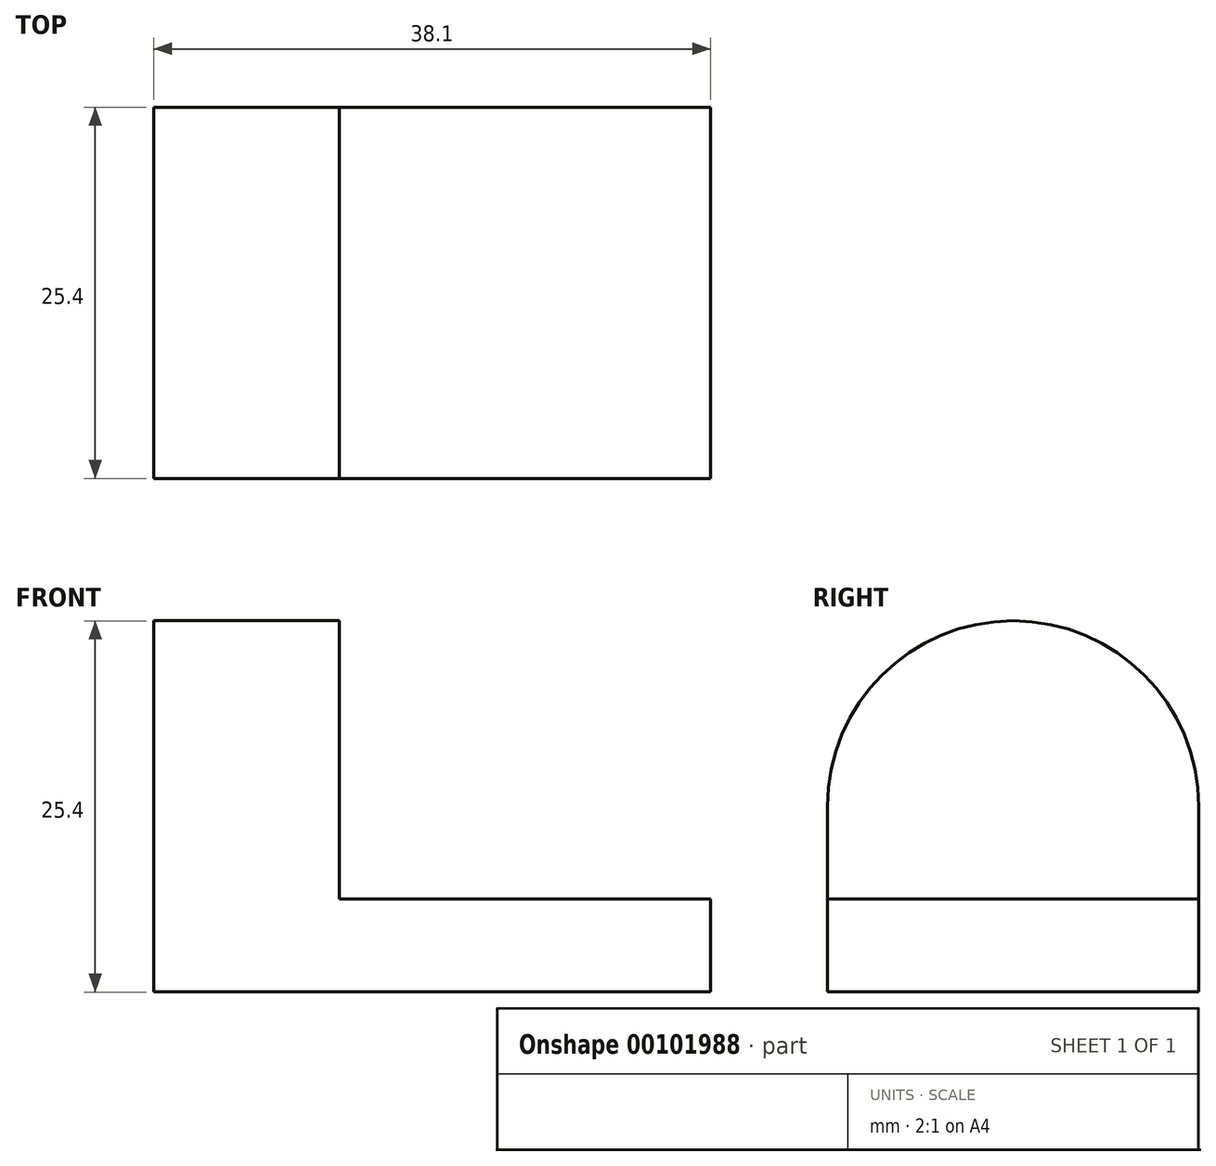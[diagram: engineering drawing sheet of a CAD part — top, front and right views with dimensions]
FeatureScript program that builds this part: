
annotation { "Feature Type Name" : "Feature", "Feature Type Description" : "" }
export const myFeature = defineFeature(function(context is Context, id is Id, definition is map)
    precondition{}
    {
        {
            var Q0;
            Q0=qCreatedBy(makeId("Front.planeOp"),FACE);
            var sketch = newSketch(context, id + "F0", { "sketchPlane" : qUnion([Q0])});
            skLineSegment(sketch, "E0", {"start": v(-16.19, 19.66) * mm, "end": v(-16.19, -5.74) * mm});
            skLineSegment(sketch, "E1", {"start": v(-16.19, -5.74) * mm, "end": v(21.91, -5.74) * mm});
            skLineSegment(sketch, "E2", {"start": v(21.91, -5.74) * mm, "end": v(21.91, 0.61) * mm});
            skLineSegment(sketch, "E3", {"start": v(21.91, 0.61) * mm, "end": v(-3.49, 0.61) * mm});
            skLineSegment(sketch, "E4", {"start": v(-3.49, 0.61) * mm, "end": v(-3.49, 19.66) * mm});
            skLineSegment(sketch, "E5", {"start": v(-3.49, 19.66) * mm, "end": v(-16.19, 19.66) * mm});
            skSolve(sketch);
        }
        {
            var Q0;
            Q0 = qSketchRegion(id + "F0", true);
            extrude(context, id + "F1", {"entities" : qUnion([Q0]), "depth" : 25.4 * mm});
        }
        {
            var Q0;
            Q0=makeQuery(id+"F1.opExtrude","CAP_EDGE",EDGE,{"disambiguationData":[OSD([sQuery(id+"F0.wireOp",EDGE,"E5")])],"isStart":false});
            var Q1;
            Q1=makeQuery(id+"F1.opExtrude","CAP_EDGE",EDGE,{"disambiguationData":[OSD([sQuery(id+"F0.wireOp",EDGE,"E5")])],"isStart":true});
            fillet(context, id + "F2", {"entities" : qUnion([Q0, Q1]), "radius" : 12.7 * mm, "tangentPropagation" : true, "allowEdgeOverflow" : false});
        }
    });
